FCSTD DOCUMENT  (FreeCAD 0.21R33694 (Git))
Label: 4hp
License: All rights reserved
LicenseURL: https://en.wikipedia.org/wiki/All_rights_reserved
objects: Sketcher::SketchObject×1, PartDesign::Body×1
note: 2 computed .brp shape members not serialized (recipe doc carries the construction recipe); baked Part::Feature solids carry a one-line shape summary decoded from their .brp

FEATURE [Sketcher::SketchObject] Sketch
  FullyConstrained = true
  MapMode = 5
  Support = -> [XY_Plane]
  sketch-geometry (14):
    g0: LineSegment StartX=0 StartY=128.5 StartZ=0 EndX=20 EndY=128.5 EndZ=0
    g1: LineSegment StartX=20 StartY=128.5 StartZ=0 EndX=20 EndY=0 EndZ=0
    g2: LineSegment StartX=20 StartY=0 StartZ=0 EndX=0 EndY=0 EndZ=0
    g3: LineSegment StartX=0 StartY=0 StartZ=0 EndX=0 EndY=128.5 EndZ=0
    g4: ArcOfCircle CenterX=6.5 CenterY=3 CenterZ=0 NormalX=0 NormalY=0 NormalZ=1 AngleXU=0 Radius=1.5 StartAngle=1.5708 EndAngle=4.71239
    g5: ArcOfCircle CenterX=8.5 CenterY=3 CenterZ=0 NormalX=0 NormalY=0 NormalZ=1 AngleXU=0 Radius=1.5 StartAngle=4.71239 EndAngle=7.85398
    g6: LineSegment StartX=6.5 StartY=1.5 StartZ=0 EndX=8.5 EndY=1.5 EndZ=0
    g7: LineSegment StartX=8.5 StartY=4.5 StartZ=0 EndX=6.5 EndY=4.5 EndZ=0
    g8: GeomPoint X=7.5 Y=1.5 Z=0
    g9: ArcOfCircle CenterX=6.5 CenterY=125.5 CenterZ=0 NormalX=0 NormalY=0 NormalZ=1 AngleXU=0 Radius=1.5 StartAngle=1.5708 EndAngle=4.71239
    g10: ArcOfCircle CenterX=8.5 CenterY=125.5 CenterZ=0 NormalX=0 NormalY=0 NormalZ=1 AngleXU=0 Radius=1.5 StartAngle=4.71239 EndAngle=7.85398
    g11: LineSegment StartX=6.5 StartY=124 StartZ=0 EndX=8.5 EndY=124 EndZ=0
    g12: LineSegment StartX=8.5 StartY=127 StartZ=0 EndX=6.5 EndY=127 EndZ=0
    g13: GeomPoint X=7.5 Y=124 Z=0
  constraints (34):
    c: Coincident(g0,g1)
    c: Coincident(g1,g2)
    c: Coincident(g2,g3)
    c: Coincident(g3,g0)
    c: Horizontal(g0)
    c: Horizontal(g2)
    c: Vertical(g1)
    c: Vertical(g3)
    c: PointOnObject(g0,g-2)
    c: PointOnObject(g1,g-1)
    c: DistanceY(g1,g1) = 128.5
    c: DistanceX(g2,g2) = 20
    c: Tangent(g4,g6) = -1.5708
    c: Tangent(g6,g5) = -1.5708
    c: Tangent(g5,g7) = -1.5708
    c: Tangent(g7,g4) = -1.5708
    c: Equal(g4,g5)
    c: Horizontal(g6)
    c: Diameter(g5) = 3
    c: Symmetric(g4,g5,g8)
    c: DistanceX(g2,g8) = 7.5
    c: DistanceY(g2,g4) = 3
    c: Tangent(g9,g11) = -1.5708
    c: Tangent(g11,g10) = -1.5708
    c: Tangent(g10,g12) = -1.5708
    c: Tangent(g12,g9) = -1.5708
    c: Equal(g9,g10)
    c: Horizontal(g11)
    c: Diameter(g10) = 3
    c: DistanceX(g6,g6) = 2
    c: DistanceX(g11,g11) = 2
    c: Distance(g9,g0) = 3
    c: Symmetric(g9,g10,g13)
    c: DistanceX(g0,g13) = 7.5
FEATURE [PartDesign::Body] Body  label="Corps"
  Group = -> [Sketch]
  Origin = -> Origin
